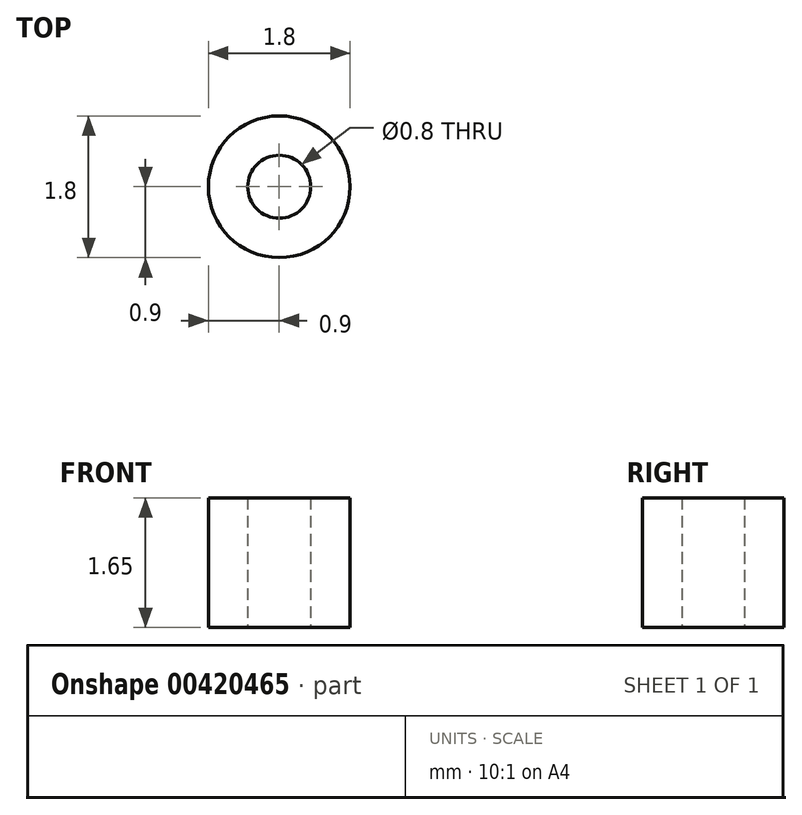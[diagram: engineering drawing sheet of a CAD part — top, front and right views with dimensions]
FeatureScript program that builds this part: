
annotation { "Feature Type Name" : "Feature", "Feature Type Description" : "" }
export const myFeature = defineFeature(function(context is Context, id is Id, definition is map)
    precondition{}
    {
        {
            var Q0;
            Q0=qCreatedBy(makeId("Top.planeOp"),FACE);
            var sketch = newSketch(context, id + "F0", { "sketchPlane" : qUnion([Q0])});
            skCircle(sketch, "E0", {"center": v(0, 0) * mm, "radius": 0.9 * mm});
            skCircle(sketch, "E1", {"center": v(0, 0) * mm, "radius": 0.4 * mm});
            skSolve(sketch);
        }
        {
            var Q0;
            Q0 = qSketchRegion(id + "F0", true);
            extrude(context, id + "F1", {"entities" : qUnion([Q0]), "depth" : 1.65 * mm});
        }
    });
